# Revit family: Урна-пепельница 114
name_source: partatom
category: Антураж
revit_build: Autodesk Revit 2017 (Build: 20160225_1515(x64)
units: mm (PartAtom-declared; Revit-internal decimal feet)

## family parameters
Всегда вертикально = Да
Источник визуального образа = Геометрия семейства
На основе рабочей плоскости = Нет
Общий = Нет
При загрузке вырезать с полостями = Нет
Точка расчета площади = Нет

## types (13) — shared parameters
ADSK_Код изделия = 7321
ADSK_Материал урны = Черный
ADSK_Наименование = Урна-пепельница 114
ADSK_Объем = 0.02 м³
ADSK_Размер_Высота = 993 мм
ADSK_Размер_Диаметр = 279 мм
ADSK_Размер_Ширина = 310 мм
URL = https://hobbyka.ru
Изготовитель = ООО "Хоббика"
Стоимость = 2100 $

## per-type parameters (varying)
| type | ADSK_Материал ведра | Высота |
| Урна-пепельница 114 (зеленый) | Зелёный RAL6029 | 993 мм |
| Урна-пепельница 114 (салатовый) | Салатовый RAL6018 | 993 мм |
| Урна-пепельница 114 (красный) | Красный RAL3020 | 993 мм |
| Урна-пепельница 114 (бордо) | Бордо RAL3004 | 993 мм |
| Урна-пепельница 114 (синий) | Синий RAL5002 | 993 мм |
| Урна-пепельница 114 (светло-серый) | Светло-серый RAL7035 | 993 мм |
| Урна-пепельница 114 (темно-серый) | Темно-серый RAL7040 | 993 мм |
| Урна-пепельница 114 (темный шоколад) | Темный шоколад | 993 мм |
| Урна-пепельница 114 (черный) | Черный | 0 мм |
| Урна-пепельница 114 (оранжевый) | Оранжевый RAL2008 | 993 мм |
| Урна-пепельница 114 (антик серебро) | Антик серебро | 993 мм |
| Урна-пепельница 114 (антик медь) | Антик медь | 993 мм |
| Урна-пепельница 114 (антик бронза) | Антик бронза | 993 мм |
